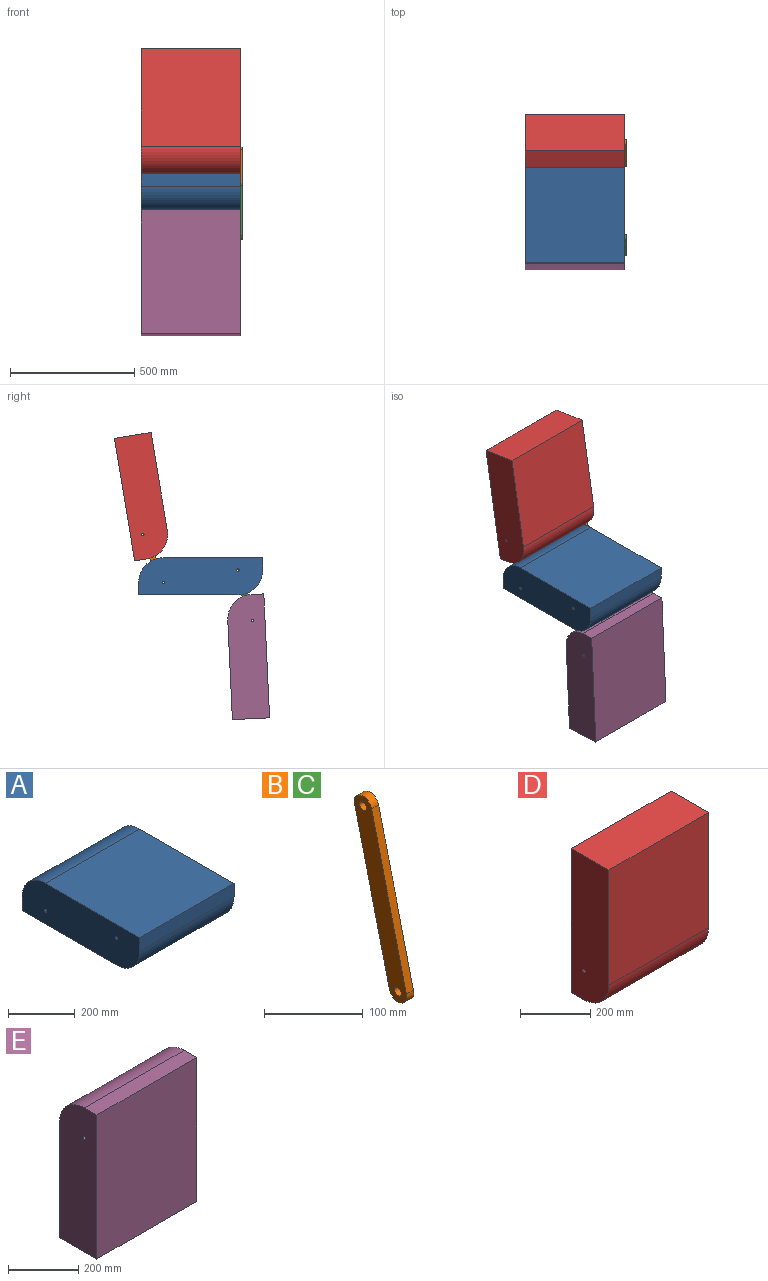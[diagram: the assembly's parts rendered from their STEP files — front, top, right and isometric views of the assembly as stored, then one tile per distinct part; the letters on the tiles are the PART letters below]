
ASSEMBLY  parts=5 mates=4
PART A: 10 faces, bbox 400x500x150 mm
  f0: plane 400x50mm, normal (0,1,0), area 20000mm2, adj f1,f6,f8,f9
  f1: cylinder r=100mm len=400mm, axis (-1,0,0), area 62831.9mm2, adj f0,f2,f8,f9
  f2: plane 400x400mm, normal (0,0,1), area 160000mm2, adj f1,f3,f8,f9
  f3: plane 400x50mm, normal (0,-1,0), area 20000mm2, adj f2,f4,f8,f9
  f4: cylinder r=100mm len=400mm, axis (-1,0,0), area 62831.9mm2, adj f3,f6,f8,f9
  f5: cylinder r=5mm len=400mm, axis (-1,0,0), area 12566.4mm2, adj f8,f9
  f6: plane 400x400mm, normal (0,0,-1), area 160000mm2, adj f0,f4,f8,f9
  f7: cylinder r=5mm len=400mm, axis (-1,0,0), area 12566.4mm2, adj f8,f9
  f8: plane 500x150mm, normal (1,0,0), area 70550.9mm2, adj f0,f1,f2,f3,f4,f5,f6,f7
  f9: plane 500x150mm, normal (-1,0,0), area 70550.9mm2, adj f0,f1,f2,f3,f4,f5,f6,f7
PART B: 8 faces, bbox 10x75x230 mm
  f0: cylinder r=12.5mm len=24.64mm, axis (-1,0,0), area 392.7mm2, adj f1,f3,f6,f7
  f1: plane 205x50mm, normal (0,-0.97,0.24), area 2110.1mm2, adj f0,f2,f6,f7
  f2: cylinder r=12.5mm len=24.64mm, axis (-1,0,0), area 392.7mm2, adj f1,f3,f6,f7
  f3: plane 205x50mm, normal (0,0.97,-0.24), area 2110.1mm2, adj f0,f2,f6,f7
  f4: cylinder r=5mm len=10mm, axis (-1,0,0), area 314.2mm2, adj f6,f7
  f5: cylinder r=5mm len=10mm, axis (-1,0,0), area 314.2mm2, adj f6,f7
  f6: plane 230x75mm, normal (1,0,0), area 5609mm2, adj f0,f1,f2,f3,f4,f5
  f7: plane 230x75mm, normal (-1,0,0), area 5609mm2, adj f0,f1,f2,f3,f4,f5
PART C: same geometry as B
PART D: 8 faces, bbox 400x150x500 mm
  f0: plane 400x50mm, normal (0,0,-1), area 20000mm2, adj f1,f5,f6,f7
  f1: plane 500x400mm, normal (0,1,0), area 200000mm2, adj f0,f2,f6,f7
  f2: plane 400x150mm, normal (0,0,1), area 60000mm2, adj f1,f3,f6,f7
  f3: plane 400x400mm, normal (0,-1,0), area 160000mm2, adj f2,f5,f6,f7
  f4: cylinder r=5mm len=400mm, axis (-1,0,0), area 12566.4mm2, adj f6,f7
  f5: cylinder r=100mm len=400mm, axis (-1,0,0), area 62831.9mm2, adj f0,f3,f6,f7
  f6: plane 500x150mm, normal (1,0,0), area 72775.4mm2, adj f0,f1,f2,f3,f4,f5
  f7: plane 500x150mm, normal (-1,0,0), area 72775.4mm2, adj f0,f1,f2,f3,f4,f5
PART E: 8 faces, bbox 400x150x500 mm
  f0: plane 400x50mm, normal (0,0,1), area 20000mm2, adj f1,f5,f6,f7
  f1: plane 500x400mm, normal (0,-1,0), area 200000mm2, adj f0,f2,f6,f7
  f2: plane 400x150mm, normal (0,0,-1), area 60000mm2, adj f1,f3,f6,f7
  f3: plane 400x400mm, normal (0,1,0), area 160000mm2, adj f2,f5,f6,f7
  f4: cylinder r=5mm len=400mm, axis (-1,0,0), area 12566.4mm2, adj f6,f7
  f5: cylinder r=100mm len=400mm, axis (-1,0,0), area 62831.9mm2, adj f0,f3,f6,f7
  f6: plane 500x150mm, normal (1,0,0), area 72775.4mm2, adj f0,f1,f2,f3,f4,f5
  f7: plane 500x150mm, normal (-1,0,0), area 72775.4mm2, adj f0,f1,f2,f3,f4,f5
PLACE A t=(-263.63,-127.69,-74.73)mm fixed
PLACE B rot(axis=(-1,0,0),9.4deg) t=(-263.63,-123.02,-12.53)mm
PLACE C rot(axis=(-1,0,0),2.7deg) t=(-263.63,-486.93,-209.36)mm
PLACE D rot(axis=(-1,0,0),9.4deg) t=(-263.63,-123.02,-12.53)mm
PLACE E rot(axis=(-1,0,0),2.7deg) t=(-263.63,-129.85,-66.41)mm
MATE revolute C.f0 <-> A.f4  axis (-1,0,0) through (136.37,-46.89,-22.06)mm
MATE fastened B.f0 <-> D.f4  axis (-1,0,0) through (136.37,335.91,122.03)mm
MATE fastened E.f4 <-> C.f2  axis (1,0,0) through (136.37,-106.42,-224.5)mm
MATE revolute A.f1 <-> B.f2  axis (1,0,0) through (136.37,253.11,-72.06)mm
